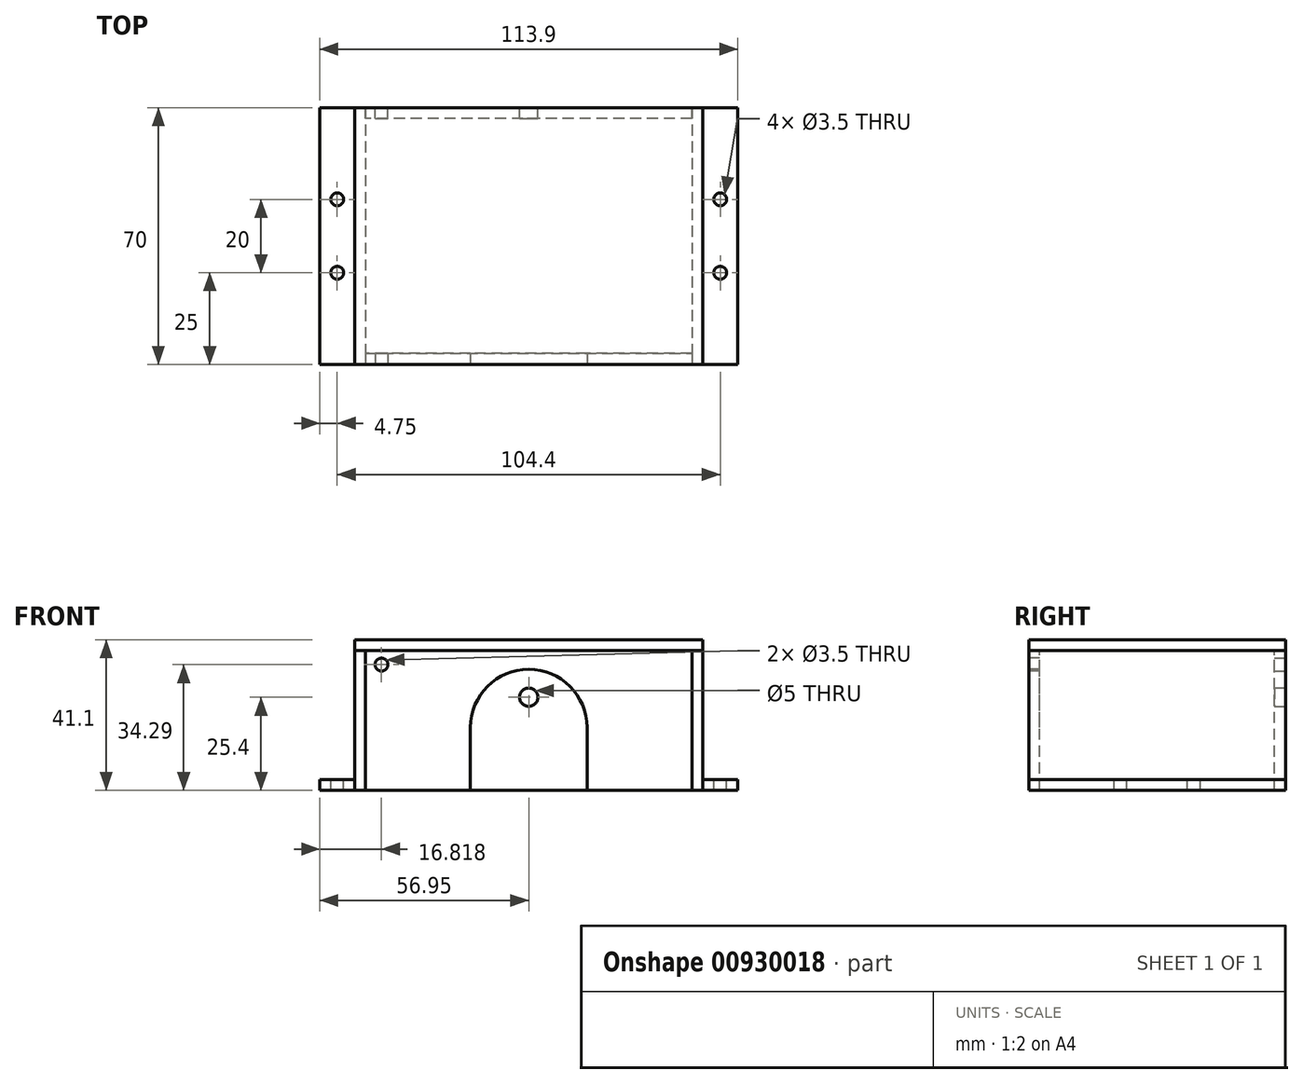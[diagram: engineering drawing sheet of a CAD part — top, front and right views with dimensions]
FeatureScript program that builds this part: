
annotation { "Feature Type Name" : "Feature", "Feature Type Description" : "" }
export const myFeature = defineFeature(function(context is Context, id is Id, definition is map)
    precondition{}
    {
        {
            assignVariable(context, id + "F0", {"name" : "length", "anyValue" : 70});
        }
        {
            assignVariable(context, id + "F1", {"name" : "thickness", "anyValue" : 3});
        }
        {
            assignVariable(context, id + "F2", {"name" : "boltD", "anyValue" : 3.5});
        }
        {
            var Q0;
            Q0=qCreatedBy(makeId("Front.planeOp"),FACE);
            var sketch = newSketch(context, id + "F3", { "sketchPlane" : qUnion([Q0])});
            skLineSegment(sketch, "E0", {"start": v(0, 0) * mm, "end": v(0, 38.1) * mm});
            skLineSegment(sketch, "E1", {"start": v(0, 38.1) * mm, "end": v(88.9, 38.1) * mm});
            skLineSegment(sketch, "E2", {"start": v(88.9, 38.1) * mm, "end": v(88.9, 0) * mm});
            skLineSegment(sketch, "E3", {"start": v(88.9, 0) * mm, "end": v(0, 0) * mm});
            skSolve(sketch);
        }
        {
            var Q0;
            Q0 = qSketchRegion(id + "F3", true);
            extrude(context, id + "F4", {"entities" : qUnion([Q0]), "oppositeDirection" : true, "depth" : getVariable(context, 'thickness') * mm, "offsetDistance" : 25.4 * mm});
        }
        {
            var Q0;
            Q0=makeQuery(id+"F4.opExtrude","CAP_FACE",FACE,{"disambiguationData":[OSD([sQuery(id+"F3.wireOp",EDGE,"E0"),sQuery(id+"F3.wireOp",EDGE,"E1"),sQuery(id+"F3.wireOp",EDGE,"E2"),sQuery(id+"F3.wireOp",EDGE,"E3")])],"isStart":true});
            var sketch = newSketch(context, id + "F5", { "sketchPlane" : qUnion([Q0])});
            skCircle(sketch, "E4", {"center": v(44.45, 25.4) * mm, "radius": 10 * mm, "construction": true});
            skCircle(sketch, "E5", {"center": v(4.32, 34.3) * mm, "radius": 1.75 * mm});
            skCircle(sketch, "E6", {"center": v(4.32, 34.3) * mm, "radius": 30 * mm, "construction": true});
            skLineSegment(sketch, "E7", {"start": v(0, 38.1) * mm, "end": v(4.32, 38.1) * mm, "construction": true});
            skLineSegment(sketch, "E8", {"start": v(4.32, 38.1) * mm, "end": v(4.32, 34.3) * mm, "construction": true});
            skLineSegment(sketch, "E9", {"start": v(44.45, 0) * mm, "end": v(44.45, 25.4) * mm, "construction": true});
            skSolve(sketch);
        }
        {
            var Q0;
            Q0 = qSketchRegion(id + "F5", true);
            extrude(context, id + "F6", {"entities" : qUnion([Q0]), "operationType" : NewBodyOperationType.REMOVE, "endBound" : BoundingType.UP_TO_NEXT, "oppositeDirection" : true, "depth" : 25.4 * mm, "offsetDistance" : 25.4 * mm});
        }
        {
            var Q0;
            Q0=qCreatedBy(makeId("Front.planeOp"),FACE);
            cPlane(context, id + "F7", {"entities" : qUnion([Q0]), "cplaneType" : CPlaneType.OFFSET, "offset" : (getVariable(context, 'length') / 2) * mm, "oppositeDirection" : true, "width" : 152.4 * mm, "height" : 152.4 * mm});
        }
        {
            var Q0;
            Q0=makeQuery(id+"F4.opExtrude","SWEPT_BODY",BODY,{"disambiguationData":[OSD([sQuery(id+"F3.wireOp",EDGE,"E0"),sQuery(id+"F3.wireOp",EDGE,"E1"),sQuery(id+"F3.wireOp",EDGE,"E2"),sQuery(id+"F3.wireOp",EDGE,"E3")])]});
            var Q1;
            Q1=qCreatedBy(id+"F7.planeOp",FACE);
            mirror(context, id + "F8", {"entities" : qUnion([Q0]), "mirrorPlane" : qUnion([Q1])});
        }
        {
            var Q0;
            Q0=qCreatedBy(makeId("Right.planeOp"),FACE);
            var Q1;
            Q1=makeQuery(id+"F4.opExtrude","CAP_VERTEX",VERTEX,{"disambiguationData":[OSD([sQuery(id+"F3.wireOp",EDGE,"E0"),sQuery(id+"F3.wireOp",EDGE,"E1")])],"isStart":true});
            cPlane(context, id + "F9", {"entities" : qUnion([Q0, Q1]), "cplaneType" : CPlaneType.PLANE_POINT, "offset" : 25.4 * mm, "width" : 152.4 * mm, "height" : 152.4 * mm});
        }
        {
            var Q0;
            Q0=qCreatedBy(id+"F9.planeOp",FACE);
            var sketch = newSketch(context, id + "F10", { "sketchPlane" : qUnion([Q0])});
            skLineSegment(sketch, "E10", {"start": v(0, 0) * mm, "end": v(0, 38.1) * mm});
            skLineSegment(sketch, "E11", {"start": v(0, 38.1) * mm, "end": v(70, 38.1) * mm});
            skLineSegment(sketch, "E12", {"start": v(70, 38.1) * mm, "end": v(70, 0) * mm});
            skLineSegment(sketch, "E13", {"start": v(70, 0) * mm, "end": v(0, 0) * mm});
            skSolve(sketch);
        }
        {
            var Q0;
            Q0 = qSketchRegion(id + "F10", true);
            extrude(context, id + "F11", {"entities" : qUnion([Q0]), "oppositeDirection" : true, "depth" : (getVariable(context, 'thickness')) * mm, "offsetDistance" : 25.4 * mm});
        }
        {
            var Q0;
            Q0=makeQuery(id+"F11.opExtrude","CAP_VERTEX",VERTEX,{"disambiguationData":[OSD([sQuery(id+"F10.wireOp",EDGE,"E10"),sQuery(id+"F10.wireOp",EDGE,"E11")])],"isStart":false});
            var Q1;
            Q1=qCreatedBy(makeId("Top.planeOp"),FACE);
            cPlane(context, id + "F12", {"entities" : qUnion([Q0, Q1]), "cplaneType" : CPlaneType.PLANE_POINT, "offset" : 25.4 * mm, "width" : 152.4 * mm, "height" : 152.4 * mm});
        }
        {
            var Q0;
            Q0=qCreatedBy(id+"F12.planeOp",FACE);
            var sketch = newSketch(context, id + "F13", { "sketchPlane" : qUnion([Q0])});
            skLineSegment(sketch, "E14", {"start": v(0, 0) * mm, "end": v(-3, 0) * mm, "construction": true});
            skLineSegment(sketch, "E15", {"start": v(-3, 0) * mm, "end": v(-3, 70) * mm});
            skLineSegment(sketch, "E16", {"start": v(-3, 70) * mm, "end": v(91.9, 70) * mm});
            skLineSegment(sketch, "E17", {"start": v(91.9, 70) * mm, "end": v(91.9, 0) * mm});
            skLineSegment(sketch, "E18", {"start": v(91.9, 0) * mm, "end": v(-3, 0) * mm});
            skSolve(sketch);
        }
        {
            var Q0;
            Q0 = qSketchRegion(id + "F13", true);
            extrude(context, id + "F14", {"entities" : qUnion([Q0]), "depth" : (getVariable(context, 'thickness')) * mm, "offsetDistance" : 25.4 * mm});
        }
        {
            var Q0;
            Q0=makeQuery(id+"F11.opExtrude","CAP_FACE",FACE,{"disambiguationData":[OSD([sQuery(id+"F10.wireOp",EDGE,"E10"),sQuery(id+"F10.wireOp",EDGE,"E11"),sQuery(id+"F10.wireOp",EDGE,"E12"),sQuery(id+"F10.wireOp",EDGE,"E13")])],"isStart":false});
            var sketch = newSketch(context, id + "F15", { "sketchPlane" : qUnion([Q0])});
            skLineSegment(sketch, "E19", {"start": v(-70, 0) * mm, "end": v(0, 0) * mm});
            skLineSegment(sketch, "E20", {"start": v(-70, 0) * mm, "end": v(-70, 3) * mm});
            skLineSegment(sketch, "E21", {"start": v(0, 3) * mm, "end": v(-70, 3) * mm});
            skLineSegment(sketch, "E22", {"start": v(0, 3) * mm, "end": v(0, 0) * mm});
            skSolve(sketch);
        }
        {
            var Q0;
            Q0 = qSketchRegion(id + "F15", true);
            extrude(context, id + "F16", {"entities" : qUnion([Q0]), "depth" : (getVariable(context, 'boltD') + 6) * mm, "offsetDistance" : 25.4 * mm});
        }
        {
            var Q0;
            Q0=qCreatedBy(makeId("Right.planeOp"),FACE);
            var Q1;
            Q1=makeQuery(id+"F4.opExtrude","SWEPT_FACE",FACE,{"disambiguationData":[OSD([sQuery(id+"F3.wireOp",EDGE,"E2")])]});
            cPlane(context, id + "F17", {"entities" : qUnion([Q0, Q1]), "cplaneType" : CPlaneType.MID_PLANE, "offset" : 25.4 * mm, "width" : 152.4 * mm, "height" : 152.4 * mm});
        }
        {
            var Q0;
            Q0=makeQuery(id+"F16.opExtrude","SWEPT_FACE",FACE,{"disambiguationData":[OSD([sQuery(id+"F15.wireOp",EDGE,"E21")])]});
            var sketch = newSketch(context, id + "F18", { "sketchPlane" : qUnion([Q0])});
            skLineSegment(sketch, "E23", {"start": v(-12.5, 35) * mm, "end": v(-3, 35) * mm, "construction": true});
            skLineSegment(sketch, "E24", {"start": v(-7.75, 35) * mm, "end": v(-7.75, 45) * mm, "construction": true});
            skCircle(sketch, "E25", {"center": v(-7.75, 45) * mm, "radius": 1.75 * mm});
            skCircle(sketch, "E26.MirrorC", {"center": v(-7.75, 25) * mm, "radius": 1.75 * mm});
            skSolve(sketch);
        }
        {
            var Q0;
            Q0 = qSketchRegion(id + "F18", true);
            extrude(context, id + "F19", {"entities" : qUnion([Q0]), "operationType" : NewBodyOperationType.REMOVE, "endBound" : BoundingType.THROUGH_ALL, "oppositeDirection" : true, "depth" : 25 * mm, "offsetDistance" : 25 * mm});
        }
        {
            var Q0;
            Q0=makeQuery(id+"F16.opExtrude","SWEPT_BODY",BODY,{"disambiguationData":[OSD([sQuery(id+"F15.wireOp",EDGE,"E19"),sQuery(id+"F15.wireOp",EDGE,"E20"),sQuery(id+"F15.wireOp",EDGE,"E21"),sQuery(id+"F15.wireOp",EDGE,"E22")])]});
            var Q1;
            Q1=makeQuery(id+"F11.opExtrude","SWEPT_BODY",BODY,{"disambiguationData":[OSD([sQuery(id+"F10.wireOp",EDGE,"E10"),sQuery(id+"F10.wireOp",EDGE,"E11"),sQuery(id+"F10.wireOp",EDGE,"E12"),sQuery(id+"F10.wireOp",EDGE,"E13")])]});
            var Q2;
            Q2=qCreatedBy(id+"F17.planeOp",FACE);
            mirror(context, id + "F20", {"entities" : qUnion([Q0, Q1]), "mirrorPlane" : qUnion([Q2])});
        }
        {
            var Q0;
            Q0=makeQuery(id+"F4.opExtrude","CAP_FACE",FACE,{"disambiguationData":[OSD([sQuery(id+"F3.wireOp",EDGE,"E0"),sQuery(id+"F3.wireOp",EDGE,"E1"),sQuery(id+"F3.wireOp",EDGE,"E2"),sQuery(id+"F3.wireOp",EDGE,"E3")])],"isStart":true});
            var sketch = newSketch(context, id + "F21", { "sketchPlane" : qUnion([Q0])});
            skLineSegment(sketch, "E27", {"start": v(44.45, 0) * mm, "end": v(44.45, 17.14) * mm, "construction": true});
            skCircle(sketch, "E28", {"center": v(44.45, 17.14) * mm, "radius": 15.87 * mm, "construction": true});
            skArc(sketch, "E29", {"start": v(60.32, 17.14) * mm, "mid": v(44.45, 33.02) * mm, "end": v(28.58, 17.15) * mm});
            skLineSegment(sketch, "E30", {"start": v(28.58, 17.15) * mm, "end": v(28.58, 0) * mm});
            skLineSegment(sketch, "E31", {"start": v(60.32, 17.14) * mm, "end": v(60.32, 0) * mm});
            skLineSegment(sketch, "E32", {"start": v(60.32, 0) * mm, "end": v(28.58, 0) * mm});
            skSolve(sketch);
        }
        {
            var Q0;
            Q0 = qSketchRegion(id + "F21", true);
            extrude(context, id + "F22", {"entities" : qUnion([Q0]), "operationType" : NewBodyOperationType.REMOVE, "endBound" : BoundingType.UP_TO_NEXT, "oppositeDirection" : true, "depth" : 25.4 * mm, "offsetDistance" : 25.4 * mm});
        }
        {
            var Q0;
            Q0=makeQuery(id+"F8.opPattern","COPY",FACE,{"derivedFrom":makeQuery(id+"F4.opExtrude","CAP_FACE",FACE,{"disambiguationData":[OSD([sQuery(id+"F3.wireOp",EDGE,"E0"),sQuery(id+"F3.wireOp",EDGE,"E1"),sQuery(id+"F3.wireOp",EDGE,"E2"),sQuery(id+"F3.wireOp",EDGE,"E3")])],"isStart":true}),"instanceName":"1"});
            var sketch = newSketch(context, id + "F23", { "sketchPlane" : qUnion([Q0])});
            skCircle(sketch, "E33", {"center": v(-44.45, 25.4) * mm, "radius": 2.5 * mm});
            skLineSegment(sketch, "E34", {"start": v(-44.45, 0) * mm, "end": v(-44.45, 25.4) * mm, "construction": true});
            skSolve(sketch);
        }
        {
            var Q0;
            Q0 = qSketchRegion(id + "F23", true);
            extrude(context, id + "F24", {"entities" : qUnion([Q0]), "operationType" : NewBodyOperationType.REMOVE, "endBound" : BoundingType.UP_TO_NEXT, "oppositeDirection" : true, "depth" : 25.4 * mm, "offsetDistance" : 25.4 * mm});
        }
    });
